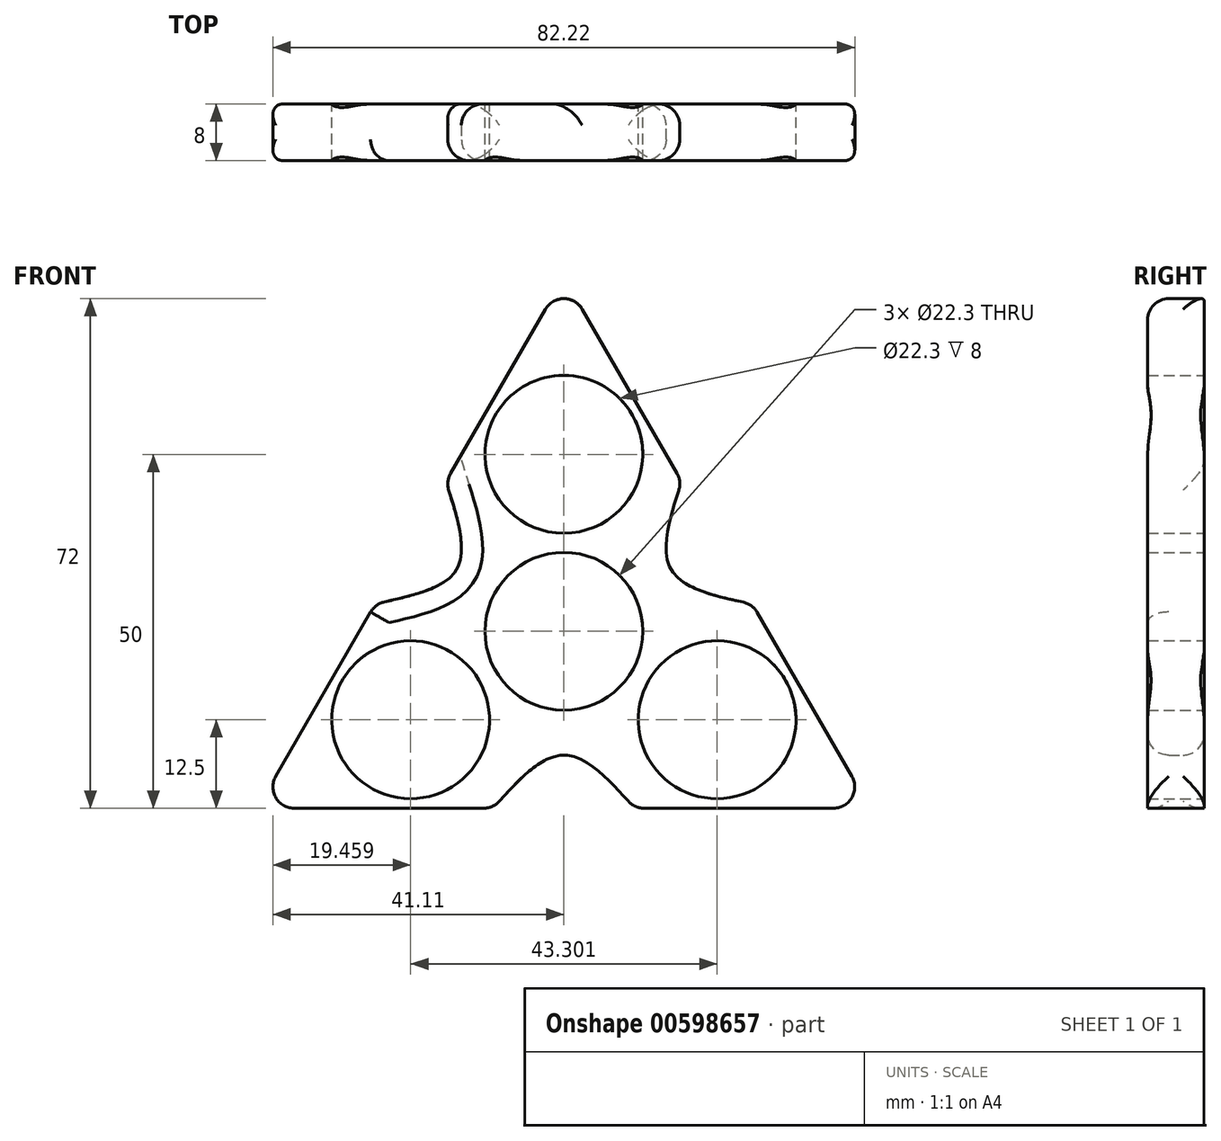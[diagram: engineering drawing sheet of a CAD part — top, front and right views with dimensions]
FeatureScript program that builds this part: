
annotation { "Feature Type Name" : "Feature", "Feature Type Description" : "" }
export const myFeature = defineFeature(function(context is Context, id is Id, definition is map)
    precondition{}
    {
        {
            var Q0;
            Q0=qCreatedBy(makeId("Front.planeOp"),FACE);
            var sketch = newSketch(context, id + "F0", { "sketchPlane" : qUnion([Q0])});
            skLineSegment(sketch, "E0", {"start": v(0, 0) * mm, "end": v(0, 50) * mm});
            skLineSegment(sketch, "E1.1.0", {"start": v(0, 0) * mm, "end": v(-43.3, -25) * mm});
            skLineSegment(sketch, "E1.2.0", {"start": v(0, 0) * mm, "end": v(43.3, -25) * mm});
            skPoint(sketch, "E1.center", {"position": v(0, 0) * mm});
            skLineSegment(sketch, "E2", {"start": v(-43.3, -25) * mm, "end": v(43.3, -25) * mm});
            skLineSegment(sketch, "E3", {"start": v(0, 50) * mm, "end": v(43.3, -25) * mm});
            skLineSegment(sketch, "E4", {"start": v(0, 50) * mm, "end": v(-43.3, -25) * mm});
            skCircle(sketch, "E5", {"center": v(0, 0) * mm, "radius": 11.15 * mm});
            skCircle(sketch, "E6", {"center": v(0, 25) * mm, "radius": 11.15 * mm});
            skCircle(sketch, "E7", {"center": v(21.65, -12.5) * mm, "radius": 11.15 * mm});
            skCircle(sketch, "E8", {"center": v(-21.65, -12.5) * mm, "radius": 11.15 * mm});
            skLineSegment(sketch, "E9", {"start": v(0, 0) * mm, "end": v(-21.65, 12.5) * mm, "construction": true});
            skLineSegment(sketch, "E10", {"start": v(-21.65, 12.5) * mm, "end": v(0, 0) * mm, "construction": true});
            skLineSegment(sketch, "E11", {"start": v(0, -25) * mm, "end": v(0, 0) * mm, "construction": true});
            skLineSegment(sketch, "E12", {"start": v(0, 0) * mm, "end": v(21.65, 12.5) * mm, "construction": true});
            skFitSpline(sketch, "E13", {"points": [v(-26.65, 3.84) * mm, v(-15.16, 8.75) * mm, v(-16.65, 21.16) * mm], "startDerivative": vector(26.44, 6.45) * mm, "endDerivative": vector(-7.93, 25.72) * mm});
            skPoint(sketch, "E14.1.0", {"position": v(-10, -25) * mm});
            skPoint(sketch, "E14.1.1", {"position": v(0, -17.5) * mm});
            skPoint(sketch, "E14.1.2", {"position": v(10, -25) * mm});
            skPoint(sketch, "E14.2.0", {"position": v(26.65, 3.84) * mm});
            skPoint(sketch, "E14.2.1", {"position": v(15.16, 8.75) * mm});
            skPoint(sketch, "E14.2.2", {"position": v(16.65, 21.16) * mm});
            skFitSpline(sketch, "E15", {"points": [v(-10, -25) * mm, v(0, -17.5) * mm, v(10, -25) * mm], "startDerivative": vector(20, 22.5) * mm, "endDerivative": vector(20, -22.5) * mm});
            skFitSpline(sketch, "E16", {"points": [v(26.65, 3.84) * mm, v(15.16, 8.75) * mm, v(16.65, 21.16) * mm], "startDerivative": vector(-29.49, 6.07) * mm, "endDerivative": vector(9.49, 28.57) * mm});
            skSolve(sketch);
        }
        {
            var Q0;
            {var subQ9=sQuery(id+"F0.wireOp",EDGE,"E16");Q0=makeQuery(id+"F0.imprint","IMPRINT",FACE,{"disambiguationData":[TD([[makeQuery(id+"F0.imprint","IMPRINT",EDGE,{"derivedFrom":subQ9}),1.0]])]});}
            var Q1;
            {var subQ3=sQuery(id+"F0.wireOp",EDGE,"E13");Q1=makeQuery(id+"F0.imprint","IMPRINT",FACE,{"disambiguationData":[TD([[makeQuery(id+"F0.imprint","IMPRINT",EDGE,{"derivedFrom":subQ3}),-1.0]])]});}
            var Q2;
            {var subQ3=sQuery(id+"F0.wireOp",EDGE,"E15");Q2=makeQuery(id+"F0.imprint","IMPRINT",FACE,{"disambiguationData":[TD([[makeQuery(id+"F0.imprint","IMPRINT",EDGE,{"derivedFrom":subQ3}),1.0]])]});}
            extrude(context, id + "F1", {"entities" : qUnion([Q0, Q1, Q2]), "depth" : 8 * mm, "offsetDistance" : 25.4 * mm});
        }
        {
            var Q0;
            {var subQ0=sQuery(id+"F0.wireOp",EDGE,"E3");Q0=makeQuery(id+"F1.opExtrude","CAP_EDGE",EDGE,{"disambiguationData":[OSD([subQ0]),TDD([makeQuery(id+"F0.imprint","IMPRINT",EDGE,{"disambiguationData":[TD([[makeQuery(id+"F0.imprint","INTERSECT",VERTEX,{"disambiguationData":[OD(1.0)],"derivedFrom":[subQ0,sQuery(id+"F0.wireOp",EDGE,"E16")]}),1.0]])],"derivedFrom":subQ0})])],"isStart":false});}
            var Q1;
            {var subQ0=sQuery(id+"F0.wireOp",EDGE,"E4");Q1=makeQuery(id+"F1.opExtrude","CAP_EDGE",EDGE,{"disambiguationData":[OSD([subQ0]),TDD([makeQuery(id+"F0.imprint","IMPRINT",EDGE,{"disambiguationData":[TD([[makeQuery(id+"F0.imprint","INTERSECT",VERTEX,{"disambiguationData":[OD(1.0)],"derivedFrom":[subQ0,sQuery(id+"F0.wireOp",EDGE,"E13")]}),1.0]])],"derivedFrom":subQ0})])],"isStart":false});}
            var Q2;
            Q2=makeQuery(id+"F1.opExtrude","CAP_EDGE",EDGE,{"disambiguationData":[OSD([sQuery(id+"F0.wireOp",EDGE,"E16")])],"isStart":false});
            var Q3;
            {var subQ0=sQuery(id+"F0.wireOp",EDGE,"E3");Q3=makeQuery(id+"F1.opExtrude","CAP_EDGE",EDGE,{"disambiguationData":[OSD([subQ0]),TDD([makeQuery(id+"F0.imprint","IMPRINT",EDGE,{"disambiguationData":[TD([[makeQuery(id+"F0.imprint","INTERSECT",VERTEX,{"disambiguationData":[OD(0.0)],"derivedFrom":[subQ0,sQuery(id+"F0.wireOp",EDGE,"E16")]}),-1.0]])],"derivedFrom":subQ0})])],"isStart":false});}
            var Q4;
            Q4=makeQuery(id+"F1.opExtrude","CAP_EDGE",EDGE,{"disambiguationData":[OSD([sQuery(id+"F0.wireOp",EDGE,"E15")])],"isStart":false});
            var Q5;
            {var subQ0=sQuery(id+"F0.wireOp",EDGE,"E2");Q5=makeQuery(id+"F1.opExtrude","CAP_EDGE",EDGE,{"disambiguationData":[OSD([subQ0]),TDD([makeQuery(id+"F0.imprint","IMPRINT",EDGE,{"disambiguationData":[TD([[makeQuery(id+"F0.imprint","INTERSECT",VERTEX,{"disambiguationData":[OD(1.0)],"derivedFrom":[subQ0,sQuery(id+"F0.wireOp",EDGE,"E15")]}),-1.0]])],"derivedFrom":subQ0})])],"isStart":false});}
            var Q6;
            {var subQ0=sQuery(id+"F0.wireOp",EDGE,"E2");Q6=makeQuery(id+"F1.opExtrude","CAP_EDGE",EDGE,{"disambiguationData":[OSD([subQ0]),TDD([makeQuery(id+"F0.imprint","IMPRINT",EDGE,{"disambiguationData":[TD([[makeQuery(id+"F0.imprint","INTERSECT",VERTEX,{"disambiguationData":[OD(0.0)],"derivedFrom":[subQ0,sQuery(id+"F0.wireOp",EDGE,"E15")]}),1.0]])],"derivedFrom":subQ0})])],"isStart":false});}
            var Q7;
            {var subQ0=sQuery(id+"F0.wireOp",EDGE,"E4");Q7=makeQuery(id+"F1.opExtrude","CAP_EDGE",EDGE,{"disambiguationData":[OSD([subQ0]),TDD([makeQuery(id+"F0.imprint","IMPRINT",EDGE,{"disambiguationData":[TD([[makeQuery(id+"F0.imprint","INTERSECT",VERTEX,{"disambiguationData":[OD(0.0)],"derivedFrom":[subQ0,sQuery(id+"F0.wireOp",EDGE,"E13")]}),-1.0]])],"derivedFrom":subQ0})])],"isStart":false});}
            var Q8;
            Q8=makeQuery(id+"F1.opExtrude","CAP_EDGE",EDGE,{"disambiguationData":[OSD([sQuery(id+"F0.wireOp",EDGE,"E13")])],"isStart":false});
            var Q9;
            {var subQ0=sQuery(id+"F0.wireOp",EDGE,"E3");Q9=makeQuery(id+"F1.opExtrude","CAP_EDGE",EDGE,{"disambiguationData":[OSD([subQ0]),TDD([makeQuery(id+"F0.imprint","IMPRINT",EDGE,{"disambiguationData":[TD([[makeQuery(id+"F0.imprint","INTERSECT",VERTEX,{"disambiguationData":[OD(1.0)],"derivedFrom":[subQ0,sQuery(id+"F0.wireOp",EDGE,"E16")]}),1.0]])],"derivedFrom":subQ0})])],"isStart":true});}
            var Q10;
            Q10=makeQuery(id+"F1.opExtrude","CAP_EDGE",EDGE,{"disambiguationData":[OSD([sQuery(id+"F0.wireOp",EDGE,"E16")])],"isStart":true});
            var Q11;
            {var subQ0=sQuery(id+"F0.wireOp",EDGE,"E3");Q11=makeQuery(id+"F1.opExtrude","CAP_EDGE",EDGE,{"disambiguationData":[OSD([subQ0]),TDD([makeQuery(id+"F0.imprint","IMPRINT",EDGE,{"disambiguationData":[TD([[makeQuery(id+"F0.imprint","INTERSECT",VERTEX,{"disambiguationData":[OD(0.0)],"derivedFrom":[subQ0,sQuery(id+"F0.wireOp",EDGE,"E16")]}),-1.0]])],"derivedFrom":subQ0})])],"isStart":true});}
            var Q12;
            {var subQ0=sQuery(id+"F0.wireOp",EDGE,"E2");Q12=makeQuery(id+"F1.opExtrude","CAP_EDGE",EDGE,{"disambiguationData":[OSD([subQ0]),TDD([makeQuery(id+"F0.imprint","IMPRINT",EDGE,{"disambiguationData":[TD([[makeQuery(id+"F0.imprint","INTERSECT",VERTEX,{"disambiguationData":[OD(1.0)],"derivedFrom":[subQ0,sQuery(id+"F0.wireOp",EDGE,"E15")]}),-1.0]])],"derivedFrom":subQ0})])],"isStart":true});}
            var Q13;
            Q13=makeQuery(id+"F1.opExtrude","CAP_EDGE",EDGE,{"disambiguationData":[OSD([sQuery(id+"F0.wireOp",EDGE,"E15")])],"isStart":true});
            var Q14;
            Q14=makeQuery(id+"F1.opExtrude","CAP_EDGE",EDGE,{"disambiguationData":[OSD([sQuery(id+"F0.wireOp",EDGE,"E13")])],"isStart":true});
            var Q15;
            {var subQ0=sQuery(id+"F0.wireOp",EDGE,"E2");Q15=makeQuery(id+"F1.opExtrude","CAP_EDGE",EDGE,{"disambiguationData":[OSD([subQ0]),TDD([makeQuery(id+"F0.imprint","IMPRINT",EDGE,{"disambiguationData":[TD([[makeQuery(id+"F0.imprint","INTERSECT",VERTEX,{"disambiguationData":[OD(0.0)],"derivedFrom":[subQ0,sQuery(id+"F0.wireOp",EDGE,"E15")]}),1.0]])],"derivedFrom":subQ0})])],"isStart":true});}
            var Q16;
            {var subQ0=sQuery(id+"F0.wireOp",EDGE,"E4");Q16=makeQuery(id+"F1.opExtrude","CAP_EDGE",EDGE,{"disambiguationData":[OSD([subQ0]),TDD([makeQuery(id+"F0.imprint","IMPRINT",EDGE,{"disambiguationData":[TD([[makeQuery(id+"F0.imprint","INTERSECT",VERTEX,{"disambiguationData":[OD(0.0)],"derivedFrom":[subQ0,sQuery(id+"F0.wireOp",EDGE,"E13")]}),-1.0]])],"derivedFrom":subQ0})])],"isStart":true});}
            var Q17;
            Q17=makeQuery(id+"F1.opExtrude","SWEPT_EDGE",EDGE,{"disambiguationData":[OSD([sQuery(id+"F0.wireOp",EDGE,"E1.1.0"),sQuery(id+"F0.wireOp",EDGE,"E2"),sQuery(id+"F0.wireOp",EDGE,"E4")])]});
            var Q18;
            {var subQ0=sQuery(id+"F0.wireOp",EDGE,"E13");var subQ1=sQuery(id+"F0.wireOp",EDGE,"E4");Q18=makeQuery(id+"F1.opExtrude","SWEPT_EDGE",EDGE,{"disambiguationData":[OSD([subQ1,subQ0]),TDD([makeQuery(id+"F0.imprint","INTERSECT",VERTEX,{"disambiguationData":[OD(0.0)],"derivedFrom":[subQ1,subQ0]})])]});}
            var Q19;
            {var subQ0=sQuery(id+"F0.wireOp",EDGE,"E13");var subQ1=sQuery(id+"F0.wireOp",EDGE,"E4");Q19=makeQuery(id+"F1.opExtrude","SWEPT_EDGE",EDGE,{"disambiguationData":[OSD([subQ1,subQ0]),TDD([makeQuery(id+"F0.imprint","INTERSECT",VERTEX,{"disambiguationData":[OD(1.0)],"derivedFrom":[subQ1,subQ0]})])]});}
            var Q20;
            Q20=makeQuery(id+"F1.opExtrude","SWEPT_EDGE",EDGE,{"disambiguationData":[OSD([sQuery(id+"F0.wireOp",EDGE,"E3"),sQuery(id+"F0.wireOp",EDGE,"E4"),sQuery(id+"F0.wireOp",EDGE,"E0")])]});
            var Q21;
            {var subQ0=sQuery(id+"F0.wireOp",EDGE,"E16");var subQ1=sQuery(id+"F0.wireOp",EDGE,"E3");Q21=makeQuery(id+"F1.opExtrude","SWEPT_EDGE",EDGE,{"disambiguationData":[OSD([subQ1,subQ0]),TDD([makeQuery(id+"F0.imprint","INTERSECT",VERTEX,{"disambiguationData":[OD(1.0)],"derivedFrom":[subQ1,subQ0]})])]});}
            var Q22;
            {var subQ0=sQuery(id+"F0.wireOp",EDGE,"E16");var subQ1=sQuery(id+"F0.wireOp",EDGE,"E3");Q22=makeQuery(id+"F1.opExtrude","SWEPT_EDGE",EDGE,{"disambiguationData":[OSD([subQ1,subQ0]),TDD([makeQuery(id+"F0.imprint","INTERSECT",VERTEX,{"disambiguationData":[OD(0.0)],"derivedFrom":[subQ1,subQ0]})])]});}
            var Q23;
            Q23=makeQuery(id+"F1.opExtrude","SWEPT_EDGE",EDGE,{"disambiguationData":[OSD([sQuery(id+"F0.wireOp",EDGE,"E2"),sQuery(id+"F0.wireOp",EDGE,"E3"),sQuery(id+"F0.wireOp",EDGE,"E1.2.0")])]});
            var Q24;
            {var subQ0=sQuery(id+"F0.wireOp",EDGE,"E15");var subQ1=sQuery(id+"F0.wireOp",EDGE,"E2");Q24=makeQuery(id+"F1.opExtrude","SWEPT_EDGE",EDGE,{"disambiguationData":[OSD([subQ1,subQ0]),TDD([makeQuery(id+"F0.imprint","INTERSECT",VERTEX,{"disambiguationData":[OD(1.0)],"derivedFrom":[subQ1,subQ0]})])]});}
            var Q25;
            {var subQ0=sQuery(id+"F0.wireOp",EDGE,"E15");var subQ1=sQuery(id+"F0.wireOp",EDGE,"E2");Q25=makeQuery(id+"F1.opExtrude","SWEPT_EDGE",EDGE,{"disambiguationData":[OSD([subQ1,subQ0]),TDD([makeQuery(id+"F0.imprint","INTERSECT",VERTEX,{"disambiguationData":[OD(0.0)],"derivedFrom":[subQ1,subQ0]})])]});}
            fillet(context, id + "F2", {"entities" : qUnion([Q0, Q1, Q2, Q3, Q4, Q5, Q6, Q7, Q8, Q9, Q10, Q11, Q12, Q13, Q14, Q15, Q16, Q17, Q18, Q19, Q20, Q21, Q22, Q23, Q24, Q25]), "radius" : 3 * mm, "tangentPropagation" : true, "allowEdgeOverflow" : false});
        }
    });
